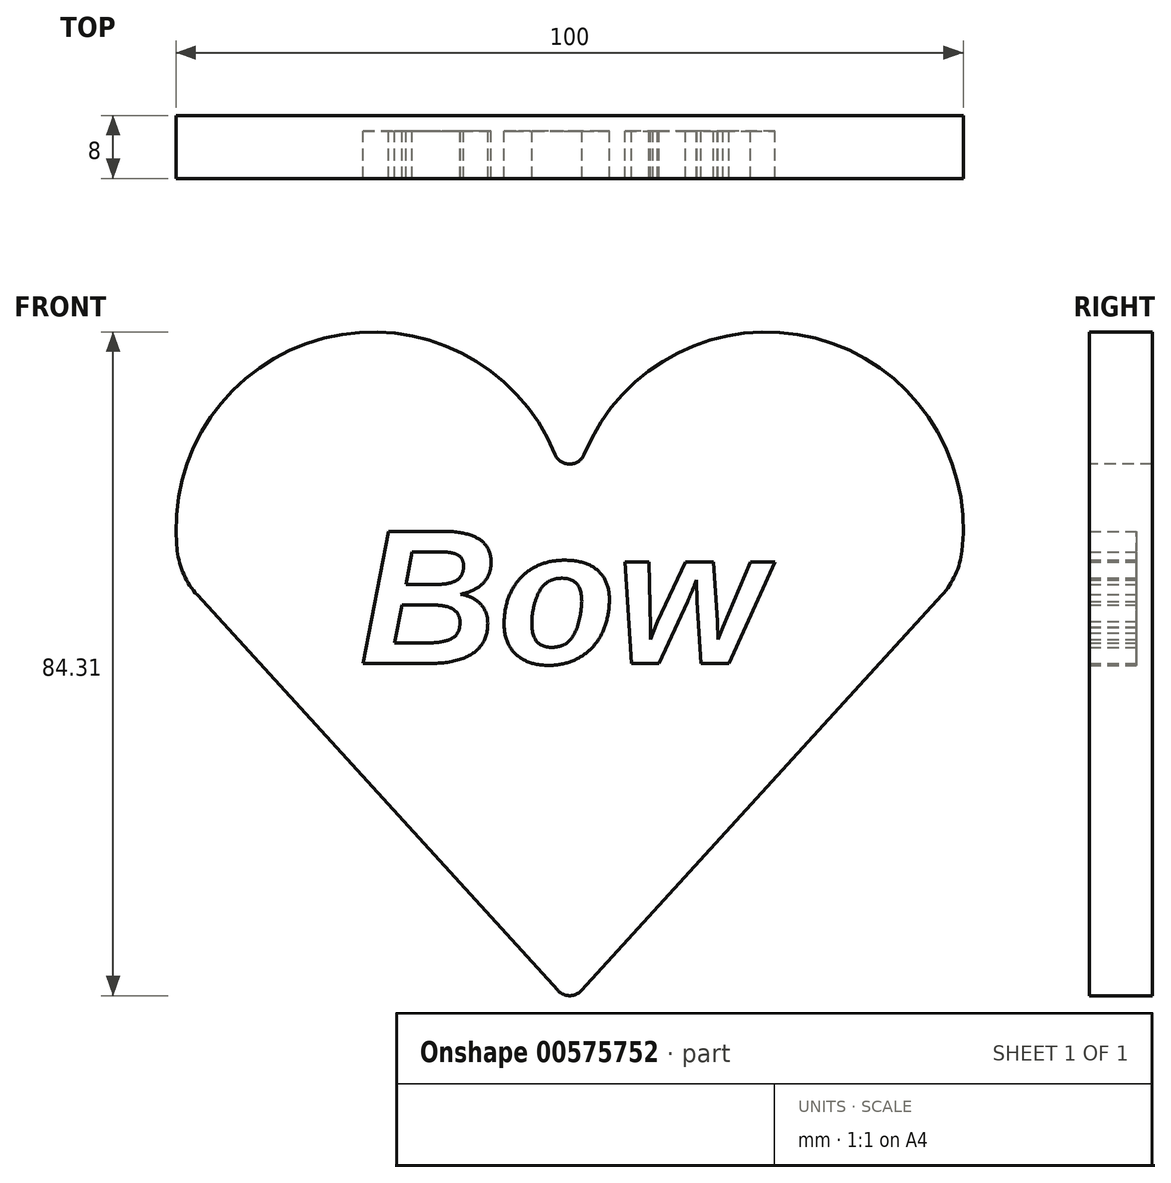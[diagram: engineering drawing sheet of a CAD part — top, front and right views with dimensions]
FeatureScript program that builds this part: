
annotation { "Feature Type Name" : "Feature", "Feature Type Description" : "" }
export const myFeature = defineFeature(function(context is Context, id is Id, definition is map)
    precondition{}
    {
        {
            var Q0;
            Q0=qCreatedBy(makeId("Front.planeOp"),FACE);
            var sketch = newSketch(context, id + "F0", { "sketchPlane" : qUnion([Q0])});
            skLineSegment(sketch, "E0", {"start": v(0, 0) * mm, "end": v(-49.17, 53.9) * mm});
            skLineSegment(sketch, "E1.MirrorCS", {"start": v(0, 0) * mm, "end": v(49.17, 53.9) * mm});
            skArc(sketch, "E2", {"start": v(0, 60.74) * mm, "mid": v(-28.44, 85.05) * mm, "end": v(-49.17, 53.9) * mm});
            skArc(sketch, "E3.MirrorCS", {"start": v(0, 60.74) * mm, "mid": v(28.44, 85.05) * mm, "end": v(49.17, 53.9) * mm});
            skPoint(sketch, "E4.orphan", {"position": v(0, 59.83) * mm});
            skSolve(sketch);
        }
        {
            var Q0;
            Q0=qCreatedBy(makeId("Front.planeOp"),FACE);
            var sketch = newSketch(context, id + "F1", { "sketchPlane" : qUnion([Q0])});
            skText(sketch, "E5", { "text": "Bow", "fontName": "Arimo-BoldItalic.ttf"});
            const initialGuessF1  = {"E5": [-0.0267, 0.04317, 1, 0, 0.01757]};
            skSetInitialGuess(sketch, initialGuessF1);
            skSolve(sketch);
        }
        {
            var Q0;
            {var subQ1=sQuery(id+"F0.wireOp",EDGE,"E0");Q0=makeQuery(id+"F0.imprint","IMPRINT",FACE,{"disambiguationData":[TD([[makeQuery(id+"F0.imprint","IMPRINT",EDGE,{"derivedFrom":subQ1}),-1.0]])]});}
            extrude(context, id + "F2", {"entities" : qUnion([Q0]), "depth" : 8 * mm, "offsetDistance" : 25 * mm});
        }
        {
            var Q0;
            Q0=makeQuery(id+"F2.opExtrude","SWEPT_EDGE",EDGE,{"disambiguationData":[OSD([sQuery(id+"F0.wireOp",EDGE,"E0"),sQuery(id+"F0.wireOp",EDGE,"E2")])]});
            var Q1;
            Q1=makeQuery(id+"F2.opExtrude","SWEPT_EDGE",EDGE,{"disambiguationData":[OSD([sQuery(id+"F0.wireOp",EDGE,"E1.MirrorCS"),sQuery(id+"F0.wireOp",EDGE,"E3.MirrorCS")])]});
            fillet(context, id + "F3", {"entities" : qUnion([Q0, Q1]), "radius" : 10 * mm, "tangentPropagation" : true, "allowEdgeOverflow" : false});
        }
        {
            var Q0;
            Q0=makeQuery(id+"F2.opExtrude","SWEPT_EDGE",EDGE,{"disambiguationData":[OSD([sQuery(id+"F0.wireOp",EDGE,"E0"),sQuery(id+"F0.wireOp",EDGE,"E1.MirrorCS")])]});
            var Q1;
            Q1=makeQuery(id+"F2.opExtrude","SWEPT_EDGE",EDGE,{"disambiguationData":[OSD([sQuery(id+"F0.wireOp",EDGE,"E2"),sQuery(id+"F0.wireOp",EDGE,"E3.MirrorCS")])]});
            fillet(context, id + "F4", {"entities" : qUnion([Q0, Q1]), "radius" : 2 * mm, "tangentPropagation" : true, "allowEdgeOverflow" : false});
        }
        {
            var Q0;
            Q0 = qSketchRegion(id + "F1", true);
            extrude(context, id + "F5", {"entities" : qUnion([Q0]), "operationType" : NewBodyOperationType.REMOVE, "depth" : 25 * mm, "offsetDistance" : 25 * mm, "hasSecondDirection" : true, "secondDirectionOppositeDirection" : false, "secondDirectionDepth" : 2 * mm});
        }
    });
